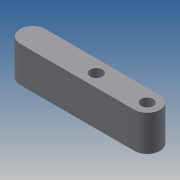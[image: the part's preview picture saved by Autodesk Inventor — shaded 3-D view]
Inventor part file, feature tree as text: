
AUTODESK INVENTOR PART (.ipt)
format: ipt  version: 2013 (Build 170138000, 138)  size: 82,432 bytes
history: native  units: mm
features: extrude x2, sketch x2
ambient origin geometry x8: Origin, YZ Plane, XZ Plane, XY Plane, X Axis, Y Axis, Z Axis, Center Point
bodies: Solid1 (feature_tree)
feature tree (4):
  extrude  "Extrusion1"  Depth=112.5mm
  extrude  "Extrusion2"  Depth=12.0mm
  sketch  "Sketch1"  dims[d0=25.0mm d2=112.5mm]
  sketch  "Sketch2"  dims[d3=35.0mm d4=0.0mm d5=12.0mm d7=50.0mm d8=35.0mm d9=0.0mm]
